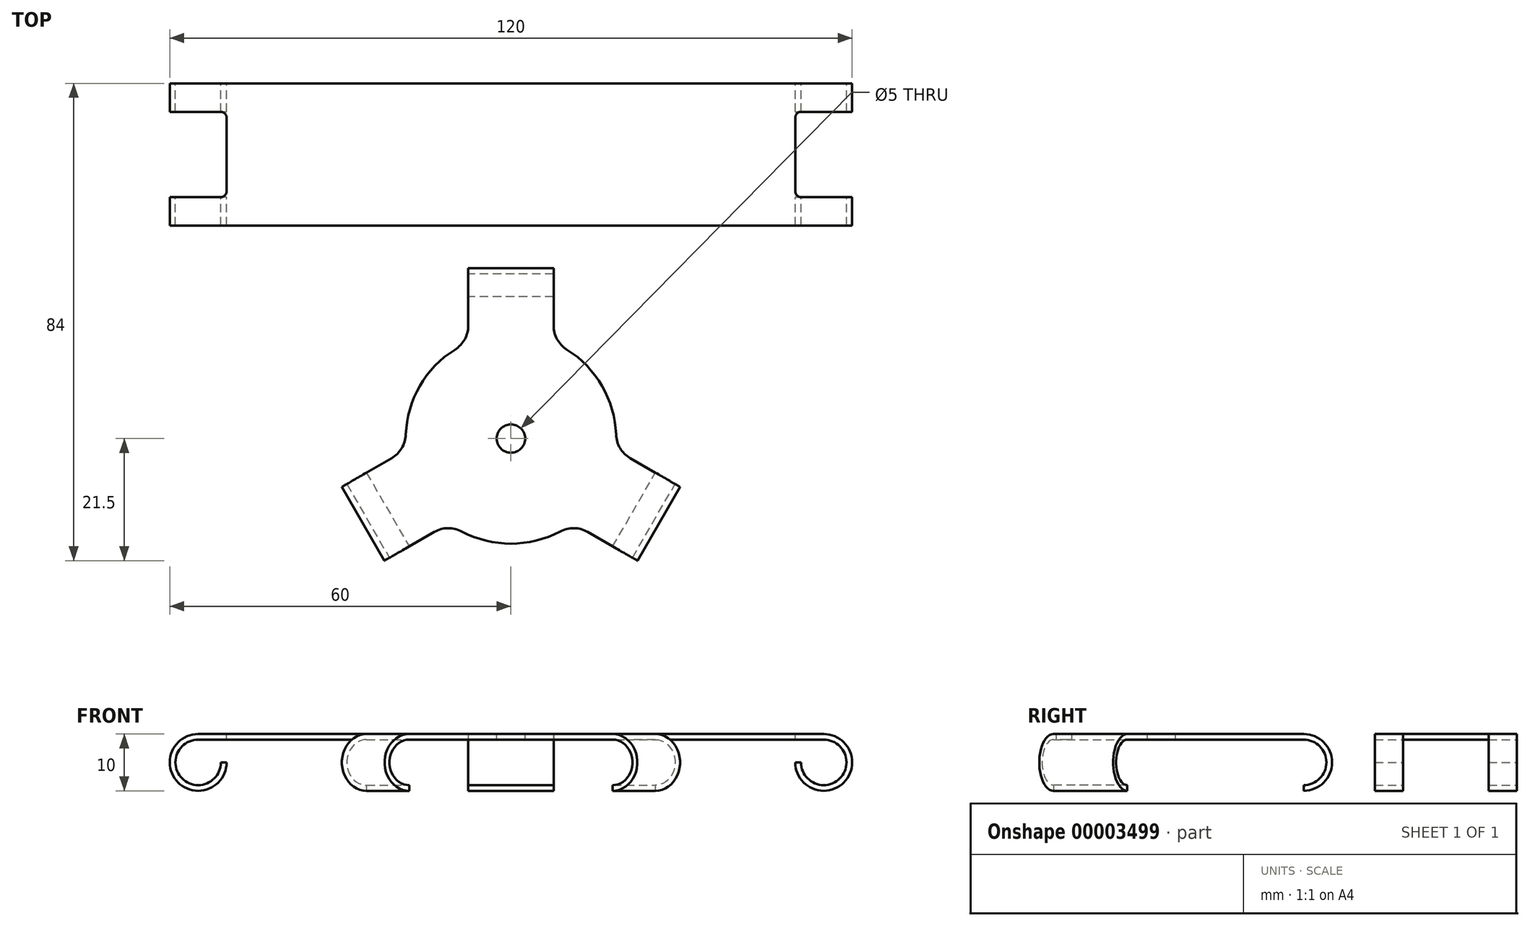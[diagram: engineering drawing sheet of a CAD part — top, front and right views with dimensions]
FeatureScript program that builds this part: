
annotation { "Feature Type Name" : "Feature", "Feature Type Description" : "" }
export const myFeature = defineFeature(function(context is Context, id is Id, definition is map)
    precondition{}
    {
        {
            var Q0;
            Q0=qCreatedBy(makeId("Front.planeOp"),FACE);
            var sketch = newSketch(context, id + "F0", { "sketchPlane" : qUnion([Q0])});
            skLineSegment(sketch, "E0", {"start": v(-55, 0) * mm, "end": v(55, 0) * mm});
            skArc(sketch, "E1", {"start": v(-55, 0) * mm, "mid": v(-58.54, -8.54) * mm, "end": v(-50, -5) * mm});
            skArc(sketch, "E2", {"start": v(55, 0) * mm, "mid": v(58.54, -8.54) * mm, "end": v(50, -5) * mm});
            skArc(sketch, "E3.0", {"start": v(55, -1) * mm, "mid": v(57.83, -7.83) * mm, "end": v(51, -5) * mm});
            skLineSegment(sketch, "E3.1", {"start": v(-55, -1) * mm, "end": v(55, -1) * mm});
            skArc(sketch, "E3.2", {"start": v(-55, -1) * mm, "mid": v(-57.83, -7.83) * mm, "end": v(-51, -5) * mm});
            skLineSegment(sketch, "E4", {"start": v(-51, -5) * mm, "end": v(-50, -5) * mm});
            skLineSegment(sketch, "E5", {"start": v(51, -5) * mm, "end": v(50, -5) * mm});
            skSolve(sketch);
        }
        {
            var Q0;
            Q0=makeQuery(id+"F0.imprint","IMPRINT",FACE,{"disambiguationData":[TD([[makeQuery(id+"F0.imprint","IMPRINT",EDGE,{"derivedFrom":sQuery(id+"F0.wireOp",EDGE,"E0")}),-1.0]])]});
            extrude(context, id + "F1", {"entities" : qUnion([Q0]), "endBound" : BoundingType.SYMMETRIC, "depth" : 25 * mm});
        }
        {
            var Q0;
            Q0=qCreatedBy(makeId("Top.planeOp"),FACE);
            var sketch = newSketch(context, id + "F2", { "sketchPlane" : qUnion([Q0])});
            skCircle(sketch, "E6", {"center": v(0, -50) * mm, "radius": 18.5 * mm});
            skLineSegment(sketch, "E7", {"start": v(0, -50) * mm, "end": v(0, -20) * mm, "construction": true});
            skLineSegment(sketch, "E8", {"start": v(0, -50) * mm, "end": v(25.98, -65) * mm, "construction": true});
            skLineSegment(sketch, "E9", {"start": v(0, -50) * mm, "end": v(-25.98, -65) * mm, "construction": true});
            skCircle(sketch, "E10", {"center": v(0, -50) * mm, "radius": 30 * mm, "construction": true});
            skLineSegment(sketch, "E11", {"start": v(-7.5, -20) * mm, "end": v(7.5, -20) * mm});
            skLineSegment(sketch, "E12", {"start": v(7.5, -20) * mm, "end": v(7.5, -45.67) * mm});
            skLineSegment(sketch, "E13", {"start": v(-7.5, -20) * mm, "end": v(-7.5, -45.67) * mm});
            skLineSegment(sketch, "E14", {"start": v(29.73, -58.5) * mm, "end": v(22.23, -71.5) * mm});
            skLineSegment(sketch, "E15", {"start": v(22.23, -71.5) * mm, "end": v(0, -58.66) * mm});
            skLineSegment(sketch, "E16", {"start": v(29.73, -58.5) * mm, "end": v(7.5, -45.67) * mm});
            skLineSegment(sketch, "E17", {"start": v(-29.73, -58.5) * mm, "end": v(-22.23, -71.5) * mm});
            skLineSegment(sketch, "E18", {"start": v(-22.23, -71.5) * mm, "end": v(0, -58.66) * mm});
            skLineSegment(sketch, "E19", {"start": v(-29.73, -58.5) * mm, "end": v(-7.5, -45.67) * mm});
            skSolve(sketch);
        }
        {
            var Q0;
            Q0=makeQuery(id+"F1.opExtrude","SWEPT_FACE",FACE,{"disambiguationData":[OSD([sQuery(id+"F0.wireOp",EDGE,"E0")])]});
            var sketch = newSketch(context, id + "F3", { "sketchPlane" : qUnion([Q0])});
            skLineSegment(sketch, "E20.rect.bottom", {"start": v(70, 7.5) * mm, "end": v(-70, 7.5) * mm});
            skLineSegment(sketch, "E20.rect.top", {"start": v(70, -7.5) * mm, "end": v(-70, -7.5) * mm});
            skLineSegment(sketch, "E20.rect.left", {"start": v(70, 7.5) * mm, "end": v(70, -7.5) * mm});
            skLineSegment(sketch, "E20.rect.right", {"start": v(-70, 7.5) * mm, "end": v(-70, -7.5) * mm});
            skPoint(sketch, "E20.rect.middle", {"position": v(0, 0) * mm});
            skLineSegment(sketch, "E21.bottom", {"start": v(-70, 7.5) * mm, "end": v(-50, 7.5) * mm});
            skLineSegment(sketch, "E21.top", {"start": v(-70, -7.5) * mm, "end": v(-50, -7.5) * mm});
            skLineSegment(sketch, "E21.right", {"start": v(-50, 7.5) * mm, "end": v(-50, -7.5) * mm});
            skLineSegment(sketch, "E22.bottom", {"start": v(70, 7.5) * mm, "end": v(50, 7.5) * mm});
            skLineSegment(sketch, "E22.top", {"start": v(70, -7.5) * mm, "end": v(50, -7.5) * mm});
            skLineSegment(sketch, "E22.right", {"start": v(50, 7.5) * mm, "end": v(50, -7.5) * mm});
            skSolve(sketch);
        }
        {
            var Q0;
            {var subQ5=sQuery(id+"F3.wireOp",EDGE,"E20.rect.right");Q0=makeQuery(id+"F3.imprint","IMPRINT",FACE,{"disambiguationData":[TD([[makeQuery(id+"F3.imprint","IMPRINT",EDGE,{"derivedFrom":subQ5}),1.0]])]});}
            var Q1;
            {var subQ5=sQuery(id+"F3.wireOp",EDGE,"E21.right");Q1=makeQuery(id+"F3.imprint","IMPRINT",FACE,{"disambiguationData":[TD([[makeQuery(id+"F3.imprint","IMPRINT",EDGE,{"derivedFrom":subQ5}),-1.0]])]});}
            var Q2;
            {var subQ5=sQuery(id+"F3.wireOp",EDGE,"E22.right");Q2=makeQuery(id+"F3.imprint","IMPRINT",FACE,{"disambiguationData":[TD([[makeQuery(id+"F3.imprint","IMPRINT",EDGE,{"derivedFrom":subQ5}),1.0]])]});}
            var Q3;
            {var subQ5=sQuery(id+"F3.wireOp",EDGE,"E20.rect.left");Q3=makeQuery(id+"F3.imprint","IMPRINT",FACE,{"disambiguationData":[TD([[makeQuery(id+"F3.imprint","IMPRINT",EDGE,{"derivedFrom":subQ5}),-1.0]])]});}
            extrude(context, id + "F4", {"entities" : qUnion([Q0, Q1, Q2, Q3]), "operationType" : NewBodyOperationType.REMOVE, "oppositeDirection" : true, "depth" : 25 * mm});
        }
        {
            var Q0;
            {var subQ0=sQuery(id+"F2.wireOp",EDGE,"E13");var subQ1=sQuery(id+"F2.wireOp",EDGE,"E6");var subQ2=makeQuery(id+"F2.imprint","INTERSECT",VERTEX,{"derivedFrom":[subQ1,subQ0]});var subQ3=sQuery(id+"F2.wireOp",EDGE,"E11");var subQ4=sQuery(id+"F2.wireOp",EDGE,"E12");var subQ5=makeQuery(id+"F2.imprint","INTERSECT",VERTEX,{"derivedFrom":[subQ1,subQ4]});var subQ6=makeQuery(id+"F2.imprint","IMPRINT",EDGE,{"disambiguationData":[TD([[subQ2,1.0]])],"derivedFrom":subQ1});var subQ12=sQuery(id+"F2.wireOp",EDGE,"E18");var subQ13=makeQuery(id+"F2.imprint","INTERSECT",VERTEX,{"derivedFrom":[subQ1,subQ12]});var subQ14=sQuery(id+"F2.wireOp",EDGE,"E17");var subQ23=sQuery(id+"F2.wireOp",EDGE,"E14");Q0=qUnion([makeQuery(id+"F2.imprint","IMPRINT",FACE,{"disambiguationData":[TD([[makeQuery(id+"F2.imprint","IMPRINT",EDGE,{"derivedFrom":subQ3}),-1.0]])]}),makeQuery(id+"F2.imprint","IMPRINT",FACE,{"disambiguationData":[TD([[makeQuery(id+"F2.imprint","IMPRINT",EDGE,{"disambiguationData":[TD([[subQ2,-1.0]])],"derivedFrom":subQ1}),1.0]])]}),makeQuery(id+"F2.imprint","IMPRINT",FACE,{"disambiguationData":[TD([[makeQuery(id+"F2.imprint","IMPRINT",EDGE,{"derivedFrom":subQ14}),1.0]])]}),makeQuery(id+"F2.imprint","IMPRINT",FACE,{"disambiguationData":[TD([[makeQuery(id+"F2.imprint","IMPRINT",EDGE,{"disambiguationData":[TD([[subQ13,-1.0]])],"derivedFrom":subQ1}),1.0]])]}),makeQuery(id+"F2.imprint","IMPRINT",FACE,{"disambiguationData":[TD([[makeQuery(id+"F2.imprint","IMPRINT",EDGE,{"derivedFrom":subQ23}),-1.0]])]}),makeQuery(id+"F2.imprint","IMPRINT",FACE,{"disambiguationData":[TD([[makeQuery(id+"F2.imprint","IMPRINT",EDGE,{"disambiguationData":[TD([[subQ5,1.0]])],"derivedFrom":subQ1}),1.0]])]}),makeQuery(id+"F2.imprint","IMPRINT",FACE,{"disambiguationData":[TD([[subQ6,1.0]])]})]);}
            extrude(context, id + "F5", {"entities" : qUnion([Q0]), "oppositeDirection" : true, "depth" : 10 * mm});
        }
        {
            var Q0;
            Q0=makeQuery(id+"F5.opExtrude","CAP_EDGE",EDGE,{"disambiguationData":[OSD([sQuery(id+"F2.wireOp",EDGE,"E17")])],"isStart":true});
            var Q1;
            Q1=makeQuery(id+"F5.opExtrude","CAP_EDGE",EDGE,{"disambiguationData":[OSD([sQuery(id+"F2.wireOp",EDGE,"E17")])],"isStart":false});
            var Q2;
            Q2=makeQuery(id+"F5.opExtrude","CAP_EDGE",EDGE,{"disambiguationData":[OSD([sQuery(id+"F2.wireOp",EDGE,"E14")])],"isStart":true});
            var Q3;
            Q3=makeQuery(id+"F5.opExtrude","CAP_EDGE",EDGE,{"disambiguationData":[OSD([sQuery(id+"F2.wireOp",EDGE,"E14")])],"isStart":false});
            var Q4;
            Q4=makeQuery(id+"F5.opExtrude","CAP_EDGE",EDGE,{"disambiguationData":[OSD([sQuery(id+"F2.wireOp",EDGE,"E11")])],"isStart":true});
            var Q5;
            Q5=makeQuery(id+"F5.opExtrude","CAP_EDGE",EDGE,{"disambiguationData":[OSD([sQuery(id+"F2.wireOp",EDGE,"E11")])],"isStart":false});
            fillet(context, id + "F6", {"entities" : qUnion([Q0, Q1, Q2, Q3, Q4, Q5]), "radius" : 5 * mm, "tangentPropagation" : true, "allowEdgeOverflow" : false});
        }
        {
            var Q0;
            Q0=makeQuery(id+"F5.opExtrude","CAP_FACE",FACE,{"disambiguationData":[OSD([sQuery(id+"F2.wireOp",EDGE,"E6"),sQuery(id+"F2.wireOp",EDGE,"E11"),sQuery(id+"F2.wireOp",EDGE,"E12"),sQuery(id+"F2.wireOp",EDGE,"E13"),sQuery(id+"F2.wireOp",EDGE,"E14"),sQuery(id+"F2.wireOp",EDGE,"E15"),sQuery(id+"F2.wireOp",EDGE,"E16"),sQuery(id+"F2.wireOp",EDGE,"E17"),sQuery(id+"F2.wireOp",EDGE,"E18"),sQuery(id+"F2.wireOp",EDGE,"E19")])],"isStart":false});
            extrude(context, id + "F7", {"entities" : qUnion([Q0]), "operationType" : NewBodyOperationType.REMOVE, "oppositeDirection" : true, "depth" : 3 * mm});
        }
        {
            var Q0;
            {var subQ0=sQuery(id+"F2.wireOp",EDGE,"E6");Q0=makeQuery(id+"F5.opExtrude","SWEPT_FACE",FACE,{"disambiguationData":[OSD([subQ0]),TDD([makeQuery(id+"F2.imprint","IMPRINT",EDGE,{"disambiguationData":[TD([[makeQuery(id+"F2.imprint","INTERSECT",VERTEX,{"derivedFrom":[subQ0,sQuery(id+"F2.wireOp",EDGE,"E12")]}),1.0]])],"derivedFrom":subQ0})])]});}
            var Q1;
            {var subQ0=sQuery(id+"F2.wireOp",EDGE,"E6");Q1=makeQuery(id+"F5.opExtrude","SWEPT_FACE",FACE,{"disambiguationData":[OSD([subQ0]),TDD([makeQuery(id+"F2.imprint","IMPRINT",EDGE,{"disambiguationData":[TD([[makeQuery(id+"F2.imprint","INTERSECT",VERTEX,{"derivedFrom":[subQ0,sQuery(id+"F2.wireOp",EDGE,"E18")]}),-1.0]])],"derivedFrom":subQ0})])]});}
            var Q2;
            Q2=makeQuery(id+"F5.opExtrude","SWEPT_FACE",FACE,{"disambiguationData":[OSD([sQuery(id+"F2.wireOp",EDGE,"E18")])]});
            var Q3;
            Q3=makeQuery(id+"F5.opExtrude","SWEPT_FACE",FACE,{"disambiguationData":[OSD([sQuery(id+"F2.wireOp",EDGE,"E12")])]});
            var Q4;
            Q4=makeQuery(id+"F5.opExtrude","SWEPT_FACE",FACE,{"disambiguationData":[OSD([sQuery(id+"F2.wireOp",EDGE,"E16")])]});
            var Q5;
            Q5=makeQuery(id+"F7.boolean.opBoolean","COPY",FACE,{"derivedFrom":makeQuery(id+"F7.opExtrude","CAP_FACE",FACE,{"disambiguationData":[OSD([sQuery(id+"F2.wireOp",EDGE,"E6"),sQuery(id+"F2.wireOp",EDGE,"E11"),sQuery(id+"F2.wireOp",EDGE,"E12"),sQuery(id+"F2.wireOp",EDGE,"E13"),sQuery(id+"F2.wireOp",EDGE,"E14"),sQuery(id+"F2.wireOp",EDGE,"E15"),sQuery(id+"F2.wireOp",EDGE,"E16"),sQuery(id+"F2.wireOp",EDGE,"E17"),sQuery(id+"F2.wireOp",EDGE,"E18"),sQuery(id+"F2.wireOp",EDGE,"E19")])],"isStart":false})});
            var Q6;
            Q6=makeQuery(id+"F5.opExtrude","SWEPT_FACE",FACE,{"disambiguationData":[OSD([sQuery(id+"F2.wireOp",EDGE,"E15")])]});
            var Q7;
            Q7=makeQuery(id+"F5.opExtrude","SWEPT_FACE",FACE,{"disambiguationData":[OSD([sQuery(id+"F2.wireOp",EDGE,"E19")])]});
            var Q8;
            {var subQ0=sQuery(id+"F2.wireOp",EDGE,"E6");Q8=makeQuery(id+"F5.opExtrude","SWEPT_FACE",FACE,{"disambiguationData":[OSD([subQ0]),TDD([makeQuery(id+"F2.imprint","IMPRINT",EDGE,{"disambiguationData":[TD([[makeQuery(id+"F2.imprint","INTERSECT",VERTEX,{"derivedFrom":[subQ0,sQuery(id+"F2.wireOp",EDGE,"E13")]}),-1.0]])],"derivedFrom":subQ0})])]});}
            var Q9;
            Q9=makeQuery(id+"F5.opExtrude","SWEPT_FACE",FACE,{"disambiguationData":[OSD([sQuery(id+"F2.wireOp",EDGE,"E13")])]});
            var Q10;
            {var subQ0=sQuery(id+"F2.wireOp",EDGE,"E6");var subQ1=sQuery(id+"F2.wireOp",EDGE,"E11");var subQ2=sQuery(id+"F2.wireOp",EDGE,"E12");var subQ3=sQuery(id+"F2.wireOp",EDGE,"E13");var subQ4=sQuery(id+"F2.wireOp",EDGE,"E14");var subQ5=sQuery(id+"F2.wireOp",EDGE,"E15");var subQ6=sQuery(id+"F2.wireOp",EDGE,"E16");var subQ7=sQuery(id+"F2.wireOp",EDGE,"E17");var subQ8=sQuery(id+"F2.wireOp",EDGE,"E18");var subQ9=sQuery(id+"F2.wireOp",EDGE,"E19");Q10=makeQuery(id+"F7.boolean.opBoolean","COPY",FACE,{"derivedFrom":makeQuery(id+"F7.opExtrude","SWEPT_FACE",FACE,{"disambiguationData":[OSD([subQ0,subQ1,subQ2,subQ3,subQ4,subQ5,subQ6,subQ7,subQ8,subQ9]),TDD([makeQuery(id+"F6.opFillet","BLEND_EDGE",EDGE,{"blendedFrom":[makeQuery(id+"F5.opExtrude","CAP_EDGE",EDGE,{"disambiguationData":[OSD([subQ4])],"isStart":false}),makeQuery(id+"F5.opExtrude","CAP_FACE",FACE,{"disambiguationData":[OSD([subQ0,subQ1,subQ2,subQ3,subQ4,subQ5,subQ6,subQ7,subQ8,subQ9])],"isStart":false})],"blendedInto":[makeQuery(id+"F5.opExtrude","CAP_FACE",FACE,{"disambiguationData":[OSD([subQ0,subQ1,subQ2,subQ3,subQ4,subQ5,subQ6,subQ7,subQ8,subQ9])],"isStart":false})]})])]})});}
            var Q11;
            {var subQ0=sQuery(id+"F2.wireOp",EDGE,"E6");var subQ1=sQuery(id+"F2.wireOp",EDGE,"E11");var subQ2=sQuery(id+"F2.wireOp",EDGE,"E12");var subQ3=sQuery(id+"F2.wireOp",EDGE,"E13");var subQ4=sQuery(id+"F2.wireOp",EDGE,"E14");var subQ5=sQuery(id+"F2.wireOp",EDGE,"E15");var subQ6=sQuery(id+"F2.wireOp",EDGE,"E16");var subQ7=sQuery(id+"F2.wireOp",EDGE,"E17");var subQ8=sQuery(id+"F2.wireOp",EDGE,"E18");var subQ9=sQuery(id+"F2.wireOp",EDGE,"E19");Q11=makeQuery(id+"F7.boolean.opBoolean","COPY",FACE,{"derivedFrom":makeQuery(id+"F7.opExtrude","SWEPT_FACE",FACE,{"disambiguationData":[OSD([subQ0,subQ1,subQ2,subQ3,subQ4,subQ5,subQ6,subQ7,subQ8,subQ9]),TDD([makeQuery(id+"F6.opFillet","BLEND_EDGE",EDGE,{"blendedFrom":[makeQuery(id+"F5.opExtrude","CAP_EDGE",EDGE,{"disambiguationData":[OSD([subQ1])],"isStart":false}),makeQuery(id+"F5.opExtrude","CAP_FACE",FACE,{"disambiguationData":[OSD([subQ0,subQ1,subQ2,subQ3,subQ4,subQ5,subQ6,subQ7,subQ8,subQ9])],"isStart":false})],"blendedInto":[makeQuery(id+"F5.opExtrude","CAP_FACE",FACE,{"disambiguationData":[OSD([subQ0,subQ1,subQ2,subQ3,subQ4,subQ5,subQ6,subQ7,subQ8,subQ9])],"isStart":false})]})])]})});}
            var Q12;
            {var subQ0=sQuery(id+"F2.wireOp",EDGE,"E6");var subQ1=sQuery(id+"F2.wireOp",EDGE,"E11");var subQ2=sQuery(id+"F2.wireOp",EDGE,"E12");var subQ3=sQuery(id+"F2.wireOp",EDGE,"E13");var subQ4=sQuery(id+"F2.wireOp",EDGE,"E14");var subQ5=sQuery(id+"F2.wireOp",EDGE,"E15");var subQ6=sQuery(id+"F2.wireOp",EDGE,"E16");var subQ7=sQuery(id+"F2.wireOp",EDGE,"E17");var subQ8=sQuery(id+"F2.wireOp",EDGE,"E18");var subQ9=sQuery(id+"F2.wireOp",EDGE,"E19");Q12=makeQuery(id+"F7.boolean.opBoolean","COPY",FACE,{"derivedFrom":makeQuery(id+"F7.opExtrude","SWEPT_FACE",FACE,{"disambiguationData":[OSD([subQ0,subQ1,subQ2,subQ3,subQ4,subQ5,subQ6,subQ7,subQ8,subQ9]),TDD([makeQuery(id+"F6.opFillet","BLEND_EDGE",EDGE,{"blendedFrom":[makeQuery(id+"F5.opExtrude","CAP_EDGE",EDGE,{"disambiguationData":[OSD([subQ7])],"isStart":false}),makeQuery(id+"F5.opExtrude","CAP_FACE",FACE,{"disambiguationData":[OSD([subQ0,subQ1,subQ2,subQ3,subQ4,subQ5,subQ6,subQ7,subQ8,subQ9])],"isStart":false})],"blendedInto":[makeQuery(id+"F5.opExtrude","CAP_FACE",FACE,{"disambiguationData":[OSD([subQ0,subQ1,subQ2,subQ3,subQ4,subQ5,subQ6,subQ7,subQ8,subQ9])],"isStart":false})]})])]})});}
            shell(context, id + "F8", {"entities" : qUnion([Q0, Q1, Q2, Q3, Q4, Q5, Q6, Q7, Q8, Q9, Q10, Q11, Q12]), "thickness" : 1 * mm});
        }
        {
            var Q0;
            Q0=makeQuery(id+"F5.opExtrude","SWEPT_EDGE",EDGE,{"disambiguationData":[OSD([sQuery(id+"F2.wireOp",EDGE,"E6"),sQuery(id+"F2.wireOp",EDGE,"E13")])]});
            var Q1;
            Q1=makeQuery(id+"F5.opExtrude","SWEPT_EDGE",EDGE,{"disambiguationData":[OSD([sQuery(id+"F2.wireOp",EDGE,"E6"),sQuery(id+"F2.wireOp",EDGE,"E19")])]});
            var Q2;
            Q2=makeQuery(id+"F5.opExtrude","SWEPT_EDGE",EDGE,{"disambiguationData":[OSD([sQuery(id+"F2.wireOp",EDGE,"E6"),sQuery(id+"F2.wireOp",EDGE,"E16")])]});
            var Q3;
            Q3=makeQuery(id+"F5.opExtrude","SWEPT_EDGE",EDGE,{"disambiguationData":[OSD([sQuery(id+"F2.wireOp",EDGE,"E6"),sQuery(id+"F2.wireOp",EDGE,"E12")])]});
            var Q4;
            Q4=makeQuery(id+"F5.opExtrude","SWEPT_EDGE",EDGE,{"disambiguationData":[OSD([sQuery(id+"F2.wireOp",EDGE,"E6"),sQuery(id+"F2.wireOp",EDGE,"E18")])]});
            var Q5;
            Q5=makeQuery(id+"F5.opExtrude","SWEPT_EDGE",EDGE,{"disambiguationData":[OSD([sQuery(id+"F2.wireOp",EDGE,"E6"),sQuery(id+"F2.wireOp",EDGE,"E15")])]});
            fillet(context, id + "F9", {"entities" : qUnion([Q0, Q1, Q2, Q3, Q4, Q5]), "radius" : 5 * mm, "tangentPropagation" : true, "allowEdgeOverflow" : false});
        }
        {
            var Q0;
            Q0=makeQuery(id+"F4.boolean.opBoolean","COPY",EDGE,{"derivedFrom":makeQuery(id+"F4.opExtrude","SWEPT_EDGE",EDGE,{"disambiguationData":[OSD([sQuery(id+"F3.wireOp",EDGE,"E20.rect.bottom"),sQuery(id+"F3.wireOp",EDGE,"E22.bottom"),sQuery(id+"F3.wireOp",EDGE,"E22.right")])]})});
            var Q1;
            Q1=makeQuery(id+"F4.boolean.opBoolean","COPY",EDGE,{"derivedFrom":makeQuery(id+"F4.opExtrude","SWEPT_EDGE",EDGE,{"disambiguationData":[OSD([sQuery(id+"F3.wireOp",EDGE,"E20.rect.top"),sQuery(id+"F3.wireOp",EDGE,"E22.top"),sQuery(id+"F3.wireOp",EDGE,"E22.right")])]})});
            var Q2;
            Q2=makeQuery(id+"F4.boolean.opBoolean","COPY",EDGE,{"derivedFrom":makeQuery(id+"F4.opExtrude","SWEPT_EDGE",EDGE,{"disambiguationData":[OSD([sQuery(id+"F3.wireOp",EDGE,"E20.rect.bottom"),sQuery(id+"F3.wireOp",EDGE,"E21.bottom"),sQuery(id+"F3.wireOp",EDGE,"E21.right")])]})});
            var Q3;
            Q3=makeQuery(id+"F4.boolean.opBoolean","COPY",EDGE,{"derivedFrom":makeQuery(id+"F4.opExtrude","SWEPT_EDGE",EDGE,{"disambiguationData":[OSD([sQuery(id+"F3.wireOp",EDGE,"E20.rect.top"),sQuery(id+"F3.wireOp",EDGE,"E21.top"),sQuery(id+"F3.wireOp",EDGE,"E21.right")])]})});
            fillet(context, id + "F10", {"entities" : qUnion([Q0, Q1, Q2, Q3]), "radius" : 1 * mm, "tangentPropagation" : true, "allowEdgeOverflow" : false});
        }
        {
            var Q0;
            Q0=makeQuery(id+"F5.opExtrude","CAP_FACE",FACE,{"disambiguationData":[OSD([sQuery(id+"F2.wireOp",EDGE,"E6"),sQuery(id+"F2.wireOp",EDGE,"E11"),sQuery(id+"F2.wireOp",EDGE,"E12"),sQuery(id+"F2.wireOp",EDGE,"E13"),sQuery(id+"F2.wireOp",EDGE,"E14"),sQuery(id+"F2.wireOp",EDGE,"E15"),sQuery(id+"F2.wireOp",EDGE,"E16"),sQuery(id+"F2.wireOp",EDGE,"E17"),sQuery(id+"F2.wireOp",EDGE,"E18"),sQuery(id+"F2.wireOp",EDGE,"E19")])],"isStart":true});
            var sketch = newSketch(context, id + "F11", { "sketchPlane" : qUnion([Q0])});
            skCircle(sketch, "E23", {"center": v(0, -50) * mm, "radius": 2.5 * mm});
            skSolve(sketch);
        }
        {
            var Q0;
            Q0=makeQuery(id+"F11.imprint","IMPRINT",FACE,{"disambiguationData":[TD([[makeQuery(id+"F11.imprint","IMPRINT",EDGE,{"derivedFrom":sQuery(id+"F11.wireOp",EDGE,"E23")}),1.0]])]});
            extrude(context, id + "F12", {"entities" : qUnion([Q0]), "operationType" : NewBodyOperationType.REMOVE, "oppositeDirection" : true, "depth" : 25 * mm});
        }
    });
